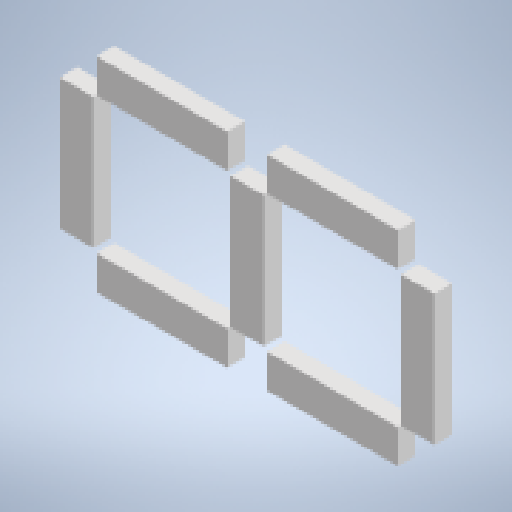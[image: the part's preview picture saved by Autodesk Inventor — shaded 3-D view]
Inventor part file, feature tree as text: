
AUTODESK INVENTOR PART (.ipt)
format: ipt  version: 2024.2 (Build 282272000, 272)  size: 166,400 bytes
history: native  units: mm
features: extrude x1, sketch x1
ambient origin geometry x8: Origin, YZ Plane, XZ Plane, XY Plane, X Axis, Y Axis, Z Axis, Center Point
bodies: Solid1 (feature_tree)
feature tree (2):
  extrude  "Extrusion1"  Depth=86.0mm
  sketch  "Sketch1"  dims[d1=100.0mm d2=86.0mm d3=86.0mm d4=17.0mm d5=17.0mm d6=66.0mm d7=66.0mm d8=86.0mm d9=9.0mm d10=0.0mm]
